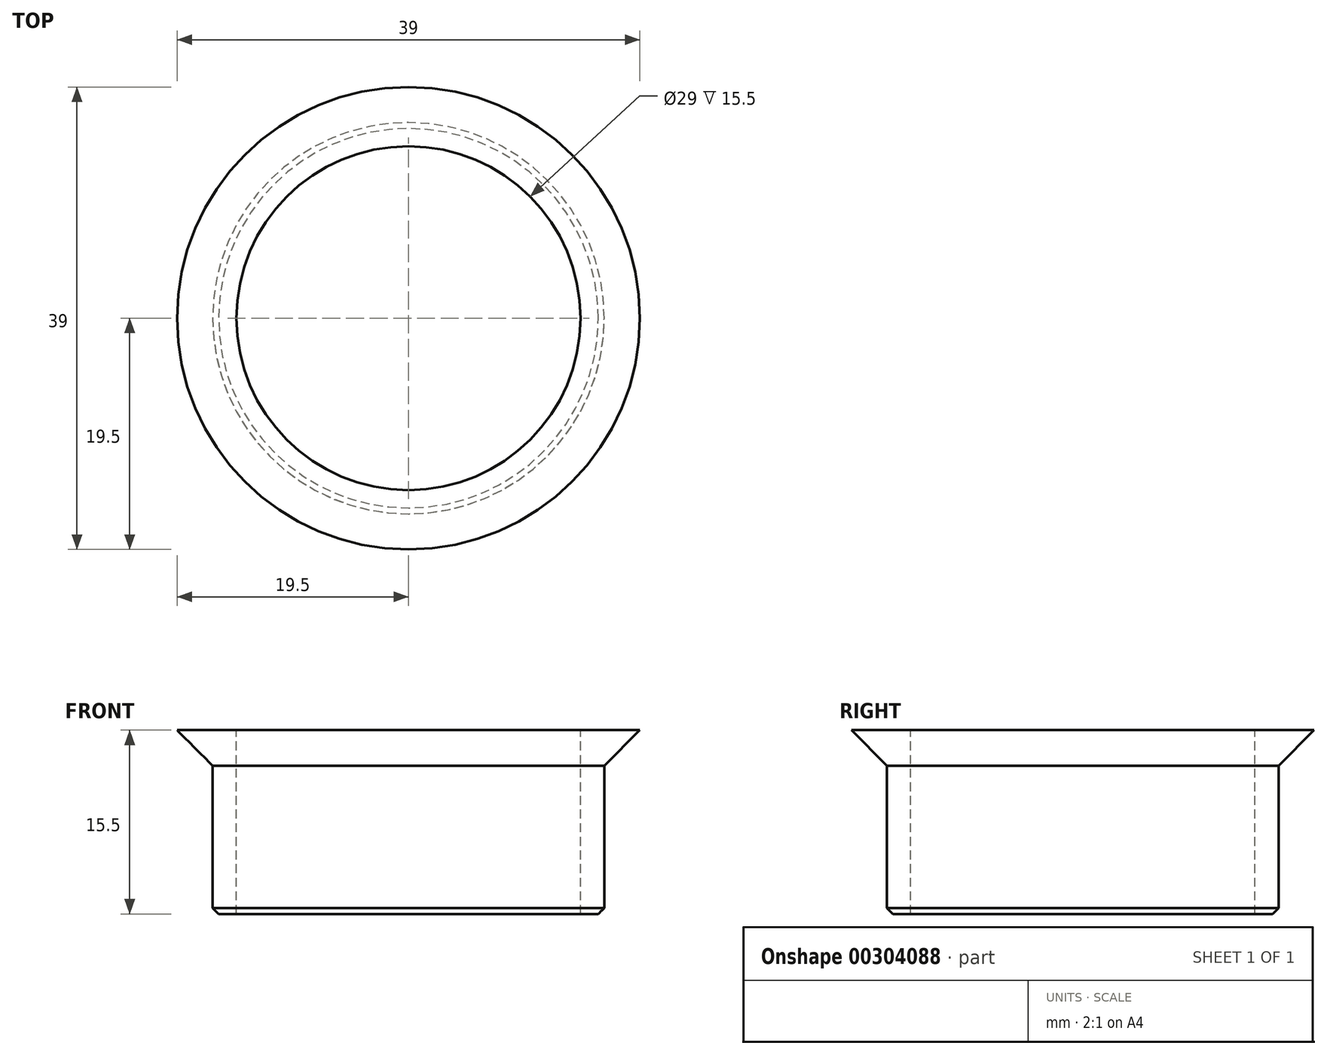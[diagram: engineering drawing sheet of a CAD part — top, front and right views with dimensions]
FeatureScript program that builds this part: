
annotation { "Feature Type Name" : "Feature", "Feature Type Description" : "" }
export const myFeature = defineFeature(function(context is Context, id is Id, definition is map)
    precondition{}
    {
        {
            var Q0;
            Q0=qCreatedBy(makeId("Front.planeOp"),FACE);
            var sketch = newSketch(context, id + "F0", { "sketchPlane" : qUnion([Q0])});
            skLineSegment(sketch, "E0", {"start": v(0, 0) * mm, "end": v(-19.5, 0) * mm});
            skLineSegment(sketch, "E1", {"start": v(-19.5, 0) * mm, "end": v(-16.5, -3) * mm});
            skLineSegment(sketch, "E2", {"start": v(-16.5, -3) * mm, "end": v(-16.5, -15.5) * mm});
            skLineSegment(sketch, "E3", {"start": v(-16.5, -15.5) * mm, "end": v(0, -15.5) * mm});
            skLineSegment(sketch, "E4", {"start": v(0, -15.5) * mm, "end": v(0, 0) * mm});
            skSolve(sketch);
        }
        {
            var Q0;
            Q0 = qSketchRegion(id + "F0", true);
            var Q1;
            Q1=sQuery(id+"F0.wireOp",EDGE,"E4");
            revolve(context, id + "F1", {"entities" : qUnion([Q0]), "axis" : qUnion([Q1]), "revolveType" : RevolveType.FULL});
        }
        {
            var Q0;
            Q0=makeQuery(id+"F1.opRevolve","SWEPT_FACE",FACE,{"disambiguationData":[OSD([sQuery(id+"F0.wireOp",EDGE,"E0")])]});
            var sketch = newSketch(context, id + "F2", { "sketchPlane" : qUnion([Q0])});
            skPoint(sketch, "E5", {"position": v(0, 0) * mm});
            skSolve(sketch);
        }
        {
            var Q0;
            Q0=sQuery(id+"F2.wireOp",VERTEX,"E5");
            var Q1;
            Q1=makeQuery(id+"F1.opRevolve","SWEPT_BODY",BODY,{"disambiguationData":[OSD([sQuery(id+"F0.wireOp",EDGE,"E0"),sQuery(id+"F0.wireOp",EDGE,"E1"),sQuery(id+"F0.wireOp",EDGE,"E2"),sQuery(id+"F0.wireOp",EDGE,"E3"),sQuery(id+"F0.wireOp",EDGE,"E4")])]});
            hole(context, id + "F3", {"style" : HoleStyle.SIMPLE, "endStyle" : HoleEndStyle.THROUGH, "holeDiameter" : 29 * mm, "tappedDepth" : 12 * mm, "tapClearance" : 3, "locations" : qUnion([Q0]), "scope" : qUnion([Q1])});
        }
        {
            var Q0;
            Q0=makeQuery(id+"F1.opRevolve","SWEPT_EDGE",EDGE,{"disambiguationData":[OSD([sQuery(id+"F0.wireOp",EDGE,"E2"),sQuery(id+"F0.wireOp",EDGE,"E3")])]});
            chamfer(context, id + "F4", {"entities" : qUnion([Q0]), "width" : 0.5 * mm, "tangentPropagation" : true});
        }
    });
